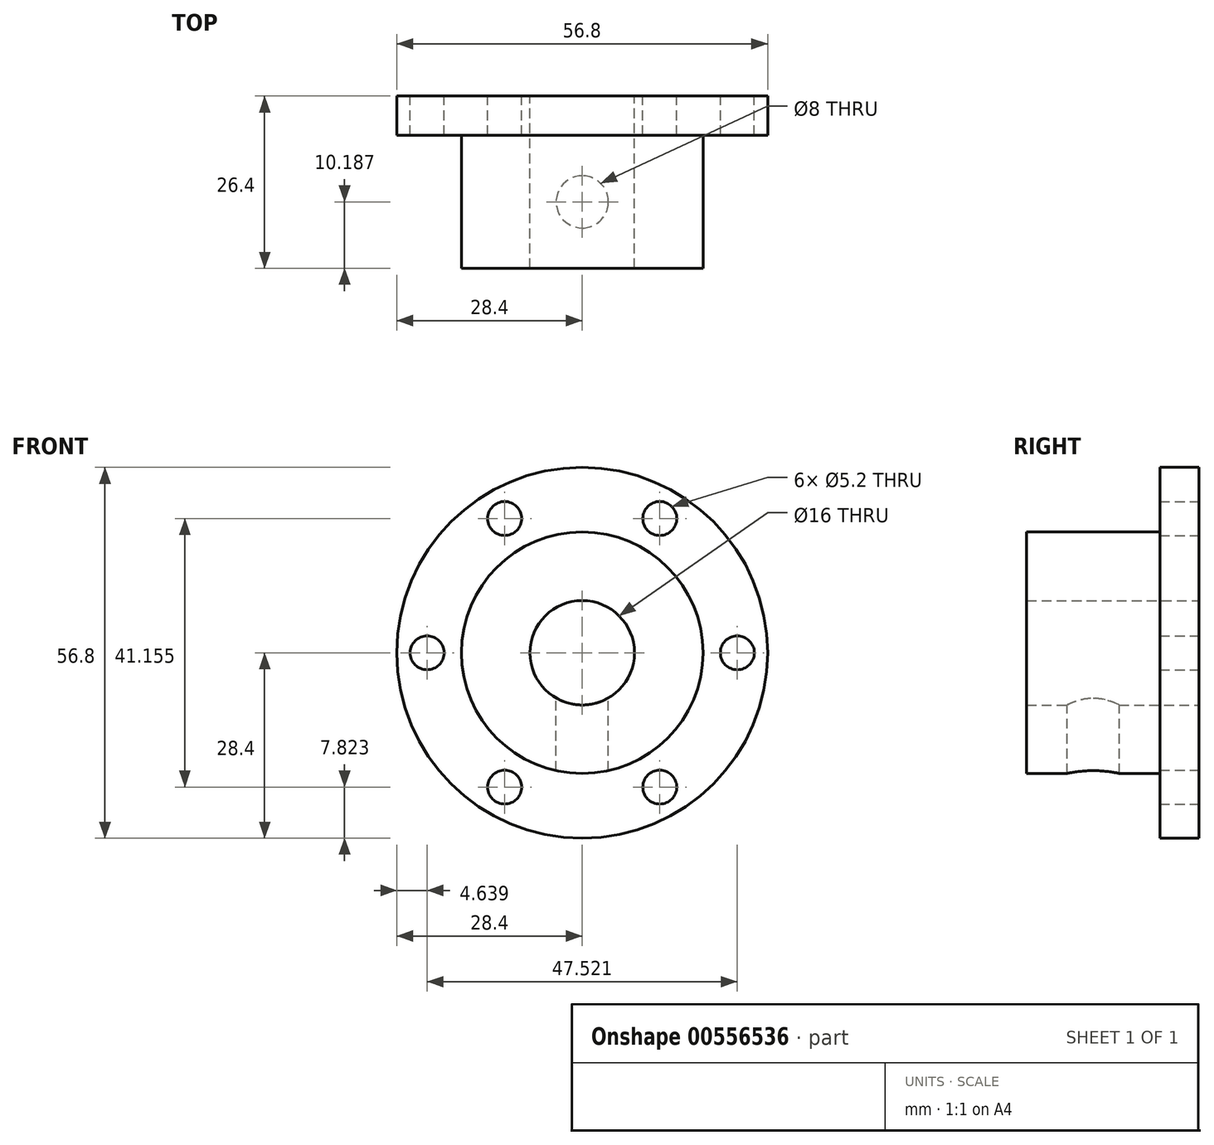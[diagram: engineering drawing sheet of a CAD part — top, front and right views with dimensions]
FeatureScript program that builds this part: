
annotation { "Feature Type Name" : "Feature", "Feature Type Description" : "" }
export const myFeature = defineFeature(function(context is Context, id is Id, definition is map)
    precondition{}
    {
        {
            var Q0;
            Q0=qCreatedBy(makeId("Front.planeOp"),FACE);
            var sketch = newSketch(context, id + "F0", { "sketchPlane" : qUnion([Q0])});
            skCircle(sketch, "E0", {"center": v(0, 0) * mm, "radius": 8 * mm});
            skSolve(sketch);
        }
        {
            var Q0;
            Q0=qCreatedBy(makeId("Front.planeOp"),FACE);
            var sketch = newSketch(context, id + "F1", { "sketchPlane" : qUnion([Q0])});
            skCircle(sketch, "E1", {"center": v(0, 0) * mm, "radius": 18.5 * mm});
            skCircle(sketch, "E2", {"center": v(0, 0) * mm, "radius": 23.75 * mm, "construction": true});
            skSolve(sketch);
        }
        {
            var Q0;
            Q0=qCreatedBy(makeId("Front.planeOp"),FACE);
            var sketch = newSketch(context, id + "F2", { "sketchPlane" : qUnion([Q0])});
            skCircle(sketch, "E3", {"center": v(0, 0) * mm, "radius": 28.4 * mm});
            skSolve(sketch);
        }
        {
            var Q0;
            Q0=qCreatedBy(makeId("Front.planeOp"),FACE);
            var sketch = newSketch(context, id + "F3", { "sketchPlane" : qUnion([Q0])});
            skCircle(sketch, "E4", {"center": v(-23.76, 0) * mm, "radius": 2.6 * mm});
            skCircle(sketch, "E5.1.0", {"center": v(-11.88, -20.58) * mm, "radius": 2.6 * mm});
            skCircle(sketch, "E5.2.0", {"center": v(11.88, -20.58) * mm, "radius": 2.6 * mm});
            skCircle(sketch, "E5.3.0", {"center": v(23.76, 0) * mm, "radius": 2.6 * mm});
            skCircle(sketch, "E5.4.0", {"center": v(11.88, 20.58) * mm, "radius": 2.6 * mm});
            skCircle(sketch, "E5.5.0", {"center": v(-11.88, 20.58) * mm, "radius": 2.6 * mm});
            skPoint(sketch, "E5.center", {"position": v(0, 0) * mm});
            skSolve(sketch);
        }
        {
            var Q0;
            Q0 = qSketchRegion(id + "F1", true);
            extrude(context, id + "F4", {"entities" : qUnion([Q0]), "depth" : 26.4 * mm, "offsetDistance" : 25 * mm});
        }
        {
            var Q0;
            Q0 = qSketchRegion(id + "F2", true);
            extrude(context, id + "F5", {"entities" : qUnion([Q0]), "operationType" : NewBodyOperationType.ADD, "depth" : 6 * mm, "offsetDistance" : 25 * mm});
        }
        {
            var Q0;
            Q0=makeQuery(id+"F0.imprint","IMPRINT",FACE,{"disambiguationData":[TD([[makeQuery(id+"F0.imprint","IMPRINT",EDGE,{"derivedFrom":sQuery(id+"F0.wireOp",EDGE,"E0")}),1.0]])]});
            var Q1;
            Q1=sQuery(id+"F0.wireOp",EDGE,"E0");
            extrude(context, id + "F6", {"entities" : qUnion([Q0]), "operationType" : NewBodyOperationType.REMOVE, "surfaceEntities" : qUnion([Q1]), "depth" : 26.4 * mm, "offsetDistance" : 25 * mm});
        }
        {
            var Q0;
            Q0 = qSketchRegion(id + "F3", true);
            extrude(context, id + "F7", {"entities" : qUnion([Q0]), "operationType" : NewBodyOperationType.REMOVE, "depth" : 6 * mm, "offsetDistance" : 25 * mm});
        }
        {
            var Q0;
            Q0=qCreatedBy(makeId("Top.planeOp"),FACE);
            var sketch = newSketch(context, id + "F8", { "sketchPlane" : qUnion([Q0])});
            skCircle(sketch, "E6", {"center": v(0, -16.21) * mm, "radius": 4 * mm});
            skSolve(sketch);
        }
        {
            var Q0;
            Q0 = qSketchRegion(id + "F8", true);
            extrude(context, id + "F9", {"entities" : qUnion([Q0]), "operationType" : NewBodyOperationType.REMOVE, "oppositeDirection" : true, "depth" : 28 * mm, "offsetDistance" : 25 * mm});
        }
    });
